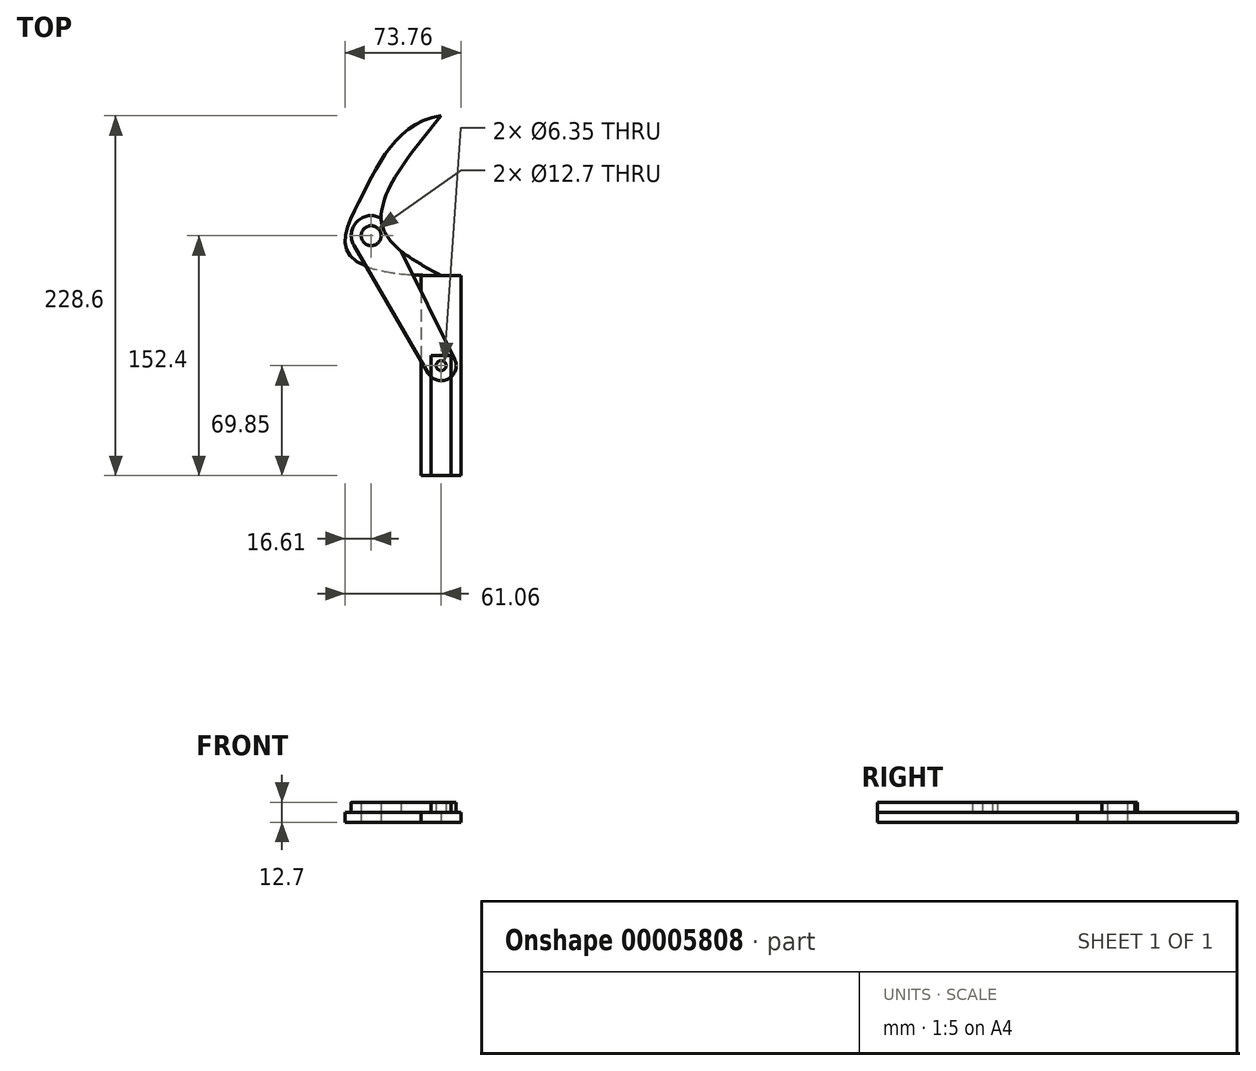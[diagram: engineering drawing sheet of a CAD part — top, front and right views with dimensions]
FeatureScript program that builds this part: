
annotation { "Feature Type Name" : "Feature", "Feature Type Description" : "" }
export const myFeature = defineFeature(function(context is Context, id is Id, definition is map)
    precondition{}
    {
        {
            var Q0;
            Q0=qCreatedBy(makeId("Top.planeOp"),FACE);
            var sketch = newSketch(context, id + "F0", { "sketchPlane" : qUnion([Q0])});
            skFitSpline(sketch, "E0", {"points": [v(0, 0) * mm, v(-37.83, 33.54) * mm, v(0, 101.6) * mm], "startDerivative": vector(-118.82, 64.53) * mm, "endDerivative": vector(110.73, 134.84) * mm});
            skFitSpline(sketch, "E1", {"points": [v(0, 101.6) * mm, v(-51.55, 48.27) * mm, v(0, 0) * mm], "startDerivative": vector(-168.19, -27.39) * mm, "endDerivative": vector(471.54, 0) * mm});
            skCircle(sketch, "E2", {"center": v(-44.45, 25.4) * mm, "radius": 6.35 * mm});
            skSolve(sketch);
        }
        {
            var Q0;
            Q0=makeQuery(id+"F0.imprint","IMPRINT",FACE,{"disambiguationData":[TD([[makeQuery(id+"F0.imprint","IMPRINT",EDGE,{"derivedFrom":sQuery(id+"F0.wireOp",EDGE,"E0")}),1.0]])]});
            extrude(context, id + "F1", {"entities" : qUnion([Q0]), "depth" : 6.35 * mm});
        }
        {
            var Q0;
            Q0=qCreatedBy(makeId("Top.planeOp"),FACE);
            var sketch = newSketch(context, id + "F2", { "sketchPlane" : qUnion([Q0])});
            skLineSegment(sketch, "E3.rect.bottom", {"start": v(12.7, 0) * mm, "end": v(-12.7, 0) * mm});
            skLineSegment(sketch, "E3.rect.top", {"start": v(12.7, -127) * mm, "end": v(-12.7, -127) * mm});
            skLineSegment(sketch, "E3.rect.left", {"start": v(12.7, 0) * mm, "end": v(12.7, -127) * mm});
            skLineSegment(sketch, "E3.rect.right", {"start": v(-12.7, 0) * mm, "end": v(-12.7, -127) * mm});
            skPoint(sketch, "E3.rect.middle", {"position": v(0, -63.5) * mm});
            skSolve(sketch);
        }
        {
            var Q0;
            Q0=makeQuery(id+"F2.imprint","IMPRINT",FACE,{"disambiguationData":[TD([[makeQuery(id+"F2.imprint","IMPRINT",EDGE,{"derivedFrom":sQuery(id+"F2.wireOp",EDGE,"E3.rect.bottom")}),1.0]])]});
            extrude(context, id + "F3", {"entities" : qUnion([Q0]), "depth" : 6.35 * mm});
        }
        {
            var Q0;
            Q0=makeQuery(id+"F3.opExtrude","CAP_FACE",FACE,{"disambiguationData":[OSD([sQuery(id+"F2.wireOp",EDGE,"E3.rect.bottom"),sQuery(id+"F2.wireOp",EDGE,"E3.rect.top"),sQuery(id+"F2.wireOp",EDGE,"E3.rect.left"),sQuery(id+"F2.wireOp",EDGE,"E3.rect.right")])],"isStart":false});
            var sketch = newSketch(context, id + "F4", { "sketchPlane" : qUnion([Q0])});
            skLineSegment(sketch, "E4.rect.bottom", {"start": v(6.35, -127) * mm, "end": v(-6.35, -127) * mm});
            skLineSegment(sketch, "E4.rect.top", {"start": v(6.35, -50.8) * mm, "end": v(-6.35, -50.8) * mm});
            skLineSegment(sketch, "E4.rect.left", {"start": v(6.35, -127) * mm, "end": v(6.35, -50.8) * mm});
            skLineSegment(sketch, "E4.rect.right", {"start": v(-6.35, -127) * mm, "end": v(-6.35, -50.8) * mm});
            skPoint(sketch, "E4.rect.middle", {"position": v(0, -88.9) * mm});
            skCircle(sketch, "E5", {"center": v(0, -57.15) * mm, "radius": 3.18 * mm});
            skSolve(sketch);
        }
        {
            var Q0;
            Q0=makeQuery(id+"F4.imprint","IMPRINT",FACE,{"disambiguationData":[TD([[makeQuery(id+"F4.imprint","IMPRINT",EDGE,{"derivedFrom":sQuery(id+"F4.wireOp",EDGE,"E4.rect.bottom")}),-1.0]])]});
            extrude(context, id + "F5", {"entities" : qUnion([Q0]), "depth" : 6.35 * mm});
        }
        {
            var Q0;
            Q0=makeQuery(id+"F1.opExtrude","CAP_FACE",FACE,{"disambiguationData":[OSD([sQuery(id+"F0.wireOp",EDGE,"E0"),sQuery(id+"F0.wireOp",EDGE,"E1"),sQuery(id+"F0.wireOp",EDGE,"E2")])],"isStart":false});
            var sketch = newSketch(context, id + "F6", { "sketchPlane" : qUnion([Q0])});
            skCircle(sketch, "E6.0", {"center": v(-44.45, 25.4) * mm, "radius": 6.35 * mm});
            skCircle(sketch, "E7.0", {"center": v(0, -57.15) * mm, "radius": 3.18 * mm});
            skLineSegment(sketch, "E8", {"start": v(-55.42, 19) * mm, "end": v(-8.23, -61.95) * mm});
            skLineSegment(sketch, "E9", {"start": v(-33.07, 31.04) * mm, "end": v(8.53, -52.92) * mm});
            skArc(sketch, "E10", {"start": v(-33.07, 31.04) * mm, "mid": v(-50.47, 36.58) * mm, "end": v(-55.42, 19) * mm});
            skArc(sketch, "E11", {"start": v(-8.23, -61.95) * mm, "mid": v(4.52, -65.54) * mm, "end": v(8.53, -52.92) * mm});
            skSolve(sketch);
        }
        {
            var Q0;
            Q0=makeQuery(id+"F6.imprint","IMPRINT",FACE,{"disambiguationData":[TD([[makeQuery(id+"F6.imprint","IMPRINT",EDGE,{"derivedFrom":sQuery(id+"F6.wireOp",EDGE,"E7.0")}),-1.0]])]});
            var Q1;
            Q1=makeQuery(id+"F6.imprint","IMPRINT",FACE,{"disambiguationData":[TD([[makeQuery(id+"F6.imprint","IMPRINT",EDGE,{"derivedFrom":sQuery(id+"F6.wireOp",EDGE,"E6.0")}),-1.0]])]});
            extrude(context, id + "F7", {"entities" : qUnion([Q0, Q1]), "depth" : 6.35 * mm});
        }
    });
